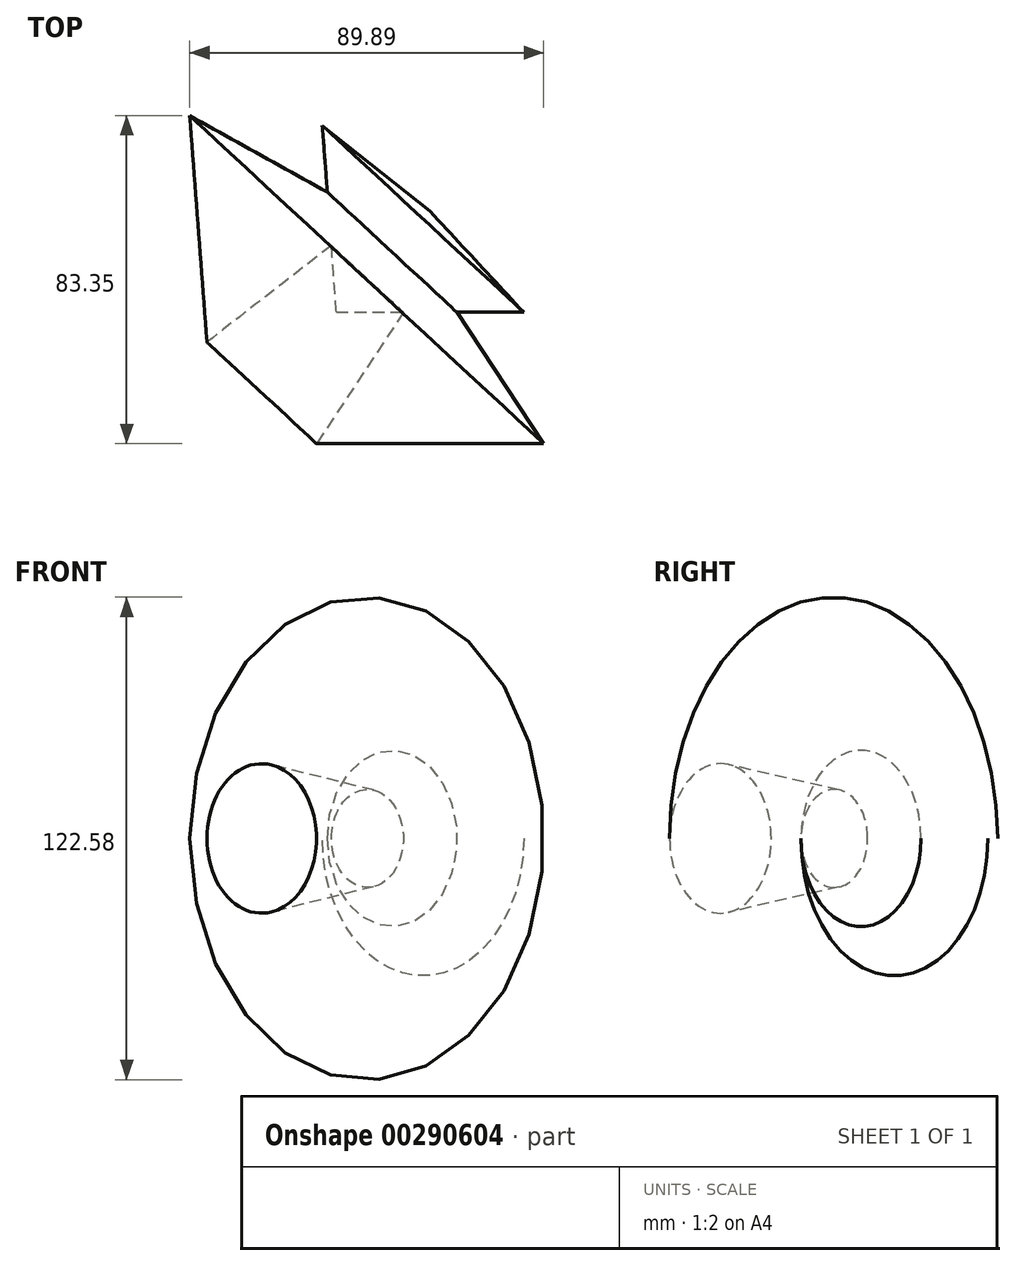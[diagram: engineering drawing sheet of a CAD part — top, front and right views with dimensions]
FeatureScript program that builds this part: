
annotation { "Feature Type Name" : "Feature", "Feature Type Description" : "" }
export const myFeature = defineFeature(function(context is Context, id is Id, definition is map)
    precondition{}
    {
        {
            var Q0;
            Q0=qCreatedBy(makeId("Top.planeOp"),FACE);
            var sketch = newSketch(context, id + "F0", { "sketchPlane" : qUnion([Q0])});
            skLineSegment(sketch, "E0", {"start": v(0, 43.34) * mm, "end": v(-23.8, 17.67) * mm});
            skLineSegment(sketch, "E1", {"start": v(-23.8, 17.67) * mm, "end": v(-6.8, 17.67) * mm});
            skLineSegment(sketch, "E2", {"start": v(-6.8, 17.67) * mm, "end": v(-28.84, -15.7) * mm});
            skLineSegment(sketch, "E3", {"start": v(-28.84, -15.7) * mm, "end": v(28.84, -15.7) * mm});
            skLineSegment(sketch, "E4", {"start": v(28.84, -15.7) * mm, "end": v(6.8, 17.67) * mm});
            skLineSegment(sketch, "E5", {"start": v(6.8, 17.67) * mm, "end": v(23.8, 17.67) * mm});
            skLineSegment(sketch, "E6", {"start": v(23.8, 17.67) * mm, "end": v(0, 43.34) * mm});
            skSolve(sketch);
        }
        {
            var Q0;
            Q0=makeQuery(id+"F0.imprint","IMPRINT",FACE,{"disambiguationData":[TD([[makeQuery(id+"F0.imprint","IMPRINT",EDGE,{"derivedFrom":sQuery(id+"F0.wireOp",EDGE,"E0")}),1.0]])]});
            var Q1;
            Q1=sQuery(id+"F0.wireOp",EDGE,"E0");
            revolve(context, id + "F1", {"entities" : qUnion([Q0]), "axis" : qUnion([Q1]), "revolveType" : RevolveType.FULL});
        }
    });
